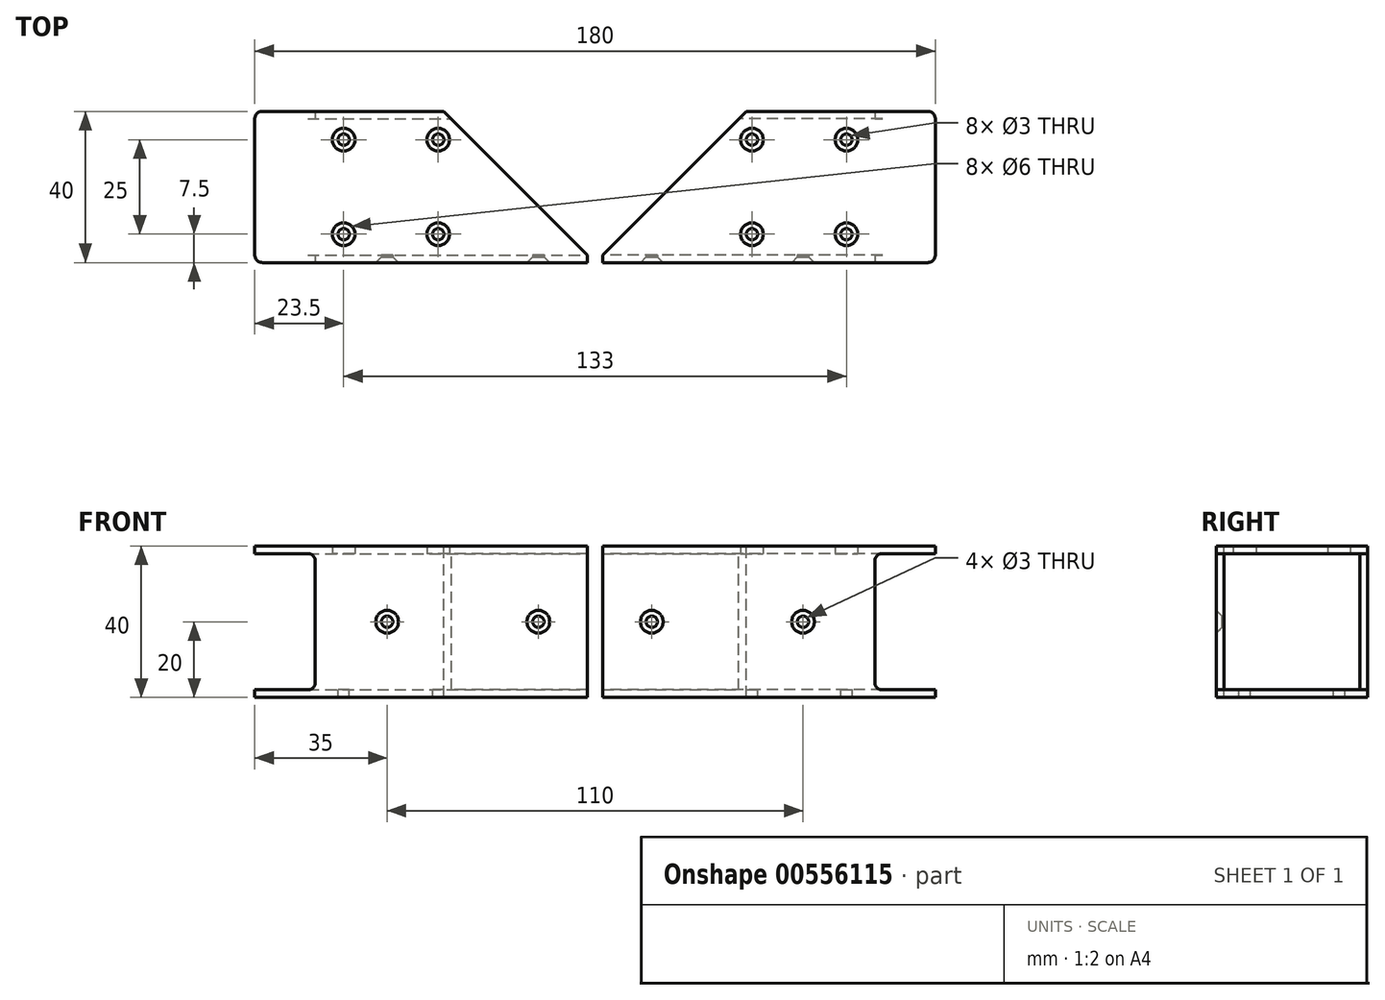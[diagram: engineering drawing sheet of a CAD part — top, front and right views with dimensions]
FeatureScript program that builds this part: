
annotation { "Feature Type Name" : "Feature", "Feature Type Description" : "" }
export const myFeature = defineFeature(function(context is Context, id is Id, definition is map)
    precondition{}
    {
        {
            var Q0;
            Q0=qCreatedBy(makeId("Right.planeOp"),FACE);
            var sketch = newSketch(context, id + "F0", { "sketchPlane" : qUnion([Q0])});
            skLineSegment(sketch, "E0.bottom", {"start": v(20, 20) * mm, "end": v(-20, 20) * mm});
            skLineSegment(sketch, "E0.top", {"start": v(20, -20) * mm, "end": v(-20, -20) * mm});
            skLineSegment(sketch, "E0.left", {"start": v(20, 20) * mm, "end": v(20, -20) * mm});
            skLineSegment(sketch, "E0.right", {"start": v(-20, 20) * mm, "end": v(-20, -20) * mm});
            skPoint(sketch, "E0.middle", {"position": v(0, 0) * mm});
            skSolve(sketch);
        }
        {
            var Q0;
            Q0=qSketchRegion(id+"F0",true);
            extrude(context, id + "F1", {"entities" : qUnion([Q0]), "oppositeDirection" : true, "depth" : 90 * mm, "offsetDistance" : 25 * mm});
        }
        {
            var Q0;
            Q0=makeQuery(id+"F1.opExtrude","CAP_FACE",FACE,{"disambiguationData":[OSD([sQuery(id+"F0.wireOp",EDGE,"E0.bottom"),sQuery(id+"F0.wireOp",EDGE,"E0.top"),sQuery(id+"F0.wireOp",EDGE,"E0.left"),sQuery(id+"F0.wireOp",EDGE,"E0.right")])],"isStart":false});
            var Q1;
            Q1=makeQuery(id+"F1.opExtrude","CAP_FACE",FACE,{"disambiguationData":[OSD([sQuery(id+"F0.wireOp",EDGE,"E0.bottom"),sQuery(id+"F0.wireOp",EDGE,"E0.top"),sQuery(id+"F0.wireOp",EDGE,"E0.left"),sQuery(id+"F0.wireOp",EDGE,"E0.right")])],"isStart":true});
            shell(context, id + "F2", {"entities" : qUnion([Q0, Q1]), "thickness" : 2 * mm});
        }
        {
            var Q0;
            Q0=makeQuery(id+"F2.opShell","OFFSET_FACE",FACE,{"disambiguationData":[OSD([sQuery(id+"F0.wireOp",EDGE,"E0.top")])]});
            var sketch = newSketch(context, id + "F3", { "sketchPlane" : qUnion([Q0])});
            skLineSegment(sketch, "E1", {"start": v(-90, 0) * mm, "end": v(0, 0) * mm, "construction": true});
            skLineSegment(sketch, "E2.bottom", {"start": v(-41.5, 12.5) * mm, "end": v(-66.5, 12.5) * mm, "construction": true});
            skLineSegment(sketch, "E2.top", {"start": v(-41.5, -12.5) * mm, "end": v(-66.5, -12.5) * mm, "construction": true});
            skLineSegment(sketch, "E2.left", {"start": v(-41.5, 12.5) * mm, "end": v(-41.5, -12.5) * mm, "construction": true});
            skLineSegment(sketch, "E2.right", {"start": v(-66.5, 12.5) * mm, "end": v(-66.5, -12.5) * mm, "construction": true});
            skPoint(sketch, "E2.middle", {"position": v(-54, 0) * mm});
            skLineSegment(sketch, "E3", {"start": v(-70, 18) * mm, "end": v(-70, -18) * mm, "construction": true});
            skSolve(sketch);
        }
        {
            var Q0;
            Q0=sQuery(id+"F3.wireOp",VERTEX,"E2.right.start");
            var Q1;
            Q1=sQuery(id+"F3.wireOp",VERTEX,"E2.top.end");
            var Q2;
            Q2=sQuery(id+"F3.wireOp",VERTEX,"E2.left.end");
            var Q3;
            Q3=sQuery(id+"F3.wireOp",VERTEX,"E2.left.start");
            var Q4;
            Q4=makeQuery(id+"F1.opExtrude","SWEPT_BODY",BODY,{"disambiguationData":[OSD([sQuery(id+"F0.wireOp",EDGE,"E0.bottom"),sQuery(id+"F0.wireOp",EDGE,"E0.top"),sQuery(id+"F0.wireOp",EDGE,"E0.left"),sQuery(id+"F0.wireOp",EDGE,"E0.right")])]});
            hole(context, id + "F4", {"style" : HoleStyle.SIMPLE, "endStyle" : HoleEndStyle.BLIND, "holeDiameter" : 3 * mm, "majorDiameter" : 5 * mm, "holeDepth" : 3 * mm, "isTappedThrough" : true, "tappedDepth" : 12 * mm, "tapClearance" : 3, "startFromSketch" : true, "locations" : qUnion([Q0, Q1, Q2, Q3]), "scope" : qUnion([Q4])});
        }
        {
            var Q0;
            Q0=sQuery(id+"F3.wireOp",VERTEX,"E2.right.start");
            var Q1;
            Q1=sQuery(id+"F3.wireOp",VERTEX,"E2.bottom.start");
            var Q2;
            Q2=sQuery(id+"F3.wireOp",VERTEX,"E2.top.end");
            var Q3;
            Q3=sQuery(id+"F3.wireOp",VERTEX,"E2.left.end");
            var Q4;
            Q4=makeQuery(id+"F1.opExtrude","SWEPT_BODY",BODY,{"disambiguationData":[OSD([sQuery(id+"F0.wireOp",EDGE,"E0.bottom"),sQuery(id+"F0.wireOp",EDGE,"E0.top"),sQuery(id+"F0.wireOp",EDGE,"E0.left"),sQuery(id+"F0.wireOp",EDGE,"E0.right")])]});
            hole(context, id + "F5", {"style" : HoleStyle.SIMPLE, "endStyle" : HoleEndStyle.BLIND, "oppositeDirection" : true, "holeDiameter" : 6 * mm, "majorDiameter" : 5 * mm, "holeDepth" : 40 * mm, "isTappedThrough" : true, "tappedDepth" : 12 * mm, "tapClearance" : 3, "locations" : qUnion([Q0, Q1, Q2, Q3]), "scope" : qUnion([Q4])});
        }
        {
            var Q0;
            Q0=makeQuery(id+"F1.opExtrude","SWEPT_FACE",FACE,{"disambiguationData":[OSD([sQuery(id+"F0.wireOp",EDGE,"E0.bottom")])]});
            var sketch = newSketch(context, id + "F6", { "sketchPlane" : qUnion([Q0])});
            skLineSegment(sketch, "E4", {"start": v(0, -20) * mm, "end": v(-40, 20) * mm});
            skLineSegment(sketch, "E5", {"start": v(-2, -20) * mm, "end": v(-2, -18) * mm});
            skSolve(sketch);
        }
        {
            var Q0;
            {var subQ1=sQuery(id+"F0.wireOp",EDGE,"E0.bottom");var subQ2=makeQuery(id+"F1.opExtrude","CAP_EDGE",EDGE,{"disambiguationData":[OSD([subQ1])],"isStart":true});Q0=makeQuery(id+"F6.imprint","IMPRINT",FACE,{"disambiguationData":[TD([[makeQuery(id+"F6.imprint","IMPRINT",EDGE,{"derivedFrom":subQ2}),-1.0]])]});}
            var Q1;
            {var subQ4=sQuery(id+"F6.wireOp",EDGE,"E5");Q1=makeQuery(id+"F6.imprint","IMPRINT",FACE,{"disambiguationData":[TD([[makeQuery(id+"F6.imprint","IMPRINT",EDGE,{"derivedFrom":subQ4}),-1.0]])]});}
            extrude(context, id + "F7", {"entities" : qUnion([Q0, Q1]), "operationType" : NewBodyOperationType.REMOVE, "endBound" : BoundingType.THROUGH_ALL, "oppositeDirection" : true, "depth" : 25 * mm, "offsetDistance" : 25 * mm});
        }
        {
            var Q0;
            Q0=makeQuery(id+"F1.opExtrude","SWEPT_FACE",FACE,{"disambiguationData":[OSD([sQuery(id+"F0.wireOp",EDGE,"E0.right")])]});
            var sketch = newSketch(context, id + "F8", { "sketchPlane" : qUnion([Q0])});
            skLineSegment(sketch, "E6", {"start": v(-70, -20) * mm, "end": v(-70, 20) * mm, "construction": true});
            skLineSegment(sketch, "E7", {"start": v(-70, 0) * mm, "end": v(-2, 0) * mm, "construction": true});
            skPoint(sketch, "E8", {"position": v(-55, 0) * mm});
            skPoint(sketch, "E9", {"position": v(-15, 0) * mm});
            skLineSegment(sketch, "E10.bottom", {"start": v(-90, -18) * mm, "end": v(-74, -18) * mm});
            skLineSegment(sketch, "E10.top", {"start": v(-90, 18) * mm, "end": v(-74, 18) * mm});
            skLineSegment(sketch, "E10.left", {"start": v(-90, -18) * mm, "end": v(-90, 18) * mm});
            skLineSegment(sketch, "E10.right", {"start": v(-74, -18) * mm, "end": v(-74, 18) * mm});
            skSolve(sketch);
        }
        {
            var Q0;
            Q0=makeQuery(id+"F8.imprint","IMPRINT",FACE,{"disambiguationData":[TD([[makeQuery(id+"F8.imprint","IMPRINT",EDGE,{"derivedFrom":sQuery(id+"F8.wireOp",EDGE,"E10.bottom")}),1.0]])]});
            extrude(context, id + "F9", {"entities" : qUnion([Q0]), "operationType" : NewBodyOperationType.REMOVE, "endBound" : BoundingType.THROUGH_ALL, "oppositeDirection" : true, "depth" : 25 * mm, "offsetDistance" : 25 * mm});
        }
        {
            var Q0;
            {var subQ0=sQuery(id+"F8.wireOp",EDGE,"E10.top");var subQ1=sQuery(id+"F0.wireOp",EDGE,"E0.right");var subQ2=sQuery(id+"F8.wireOp",EDGE,"E10.right");Q0=makeQuery(id+"F9.boolean.opBoolean","COPY",EDGE,{"disambiguationData":[TD([makeQuery(id+"F1.opExtrude","SWEPT_FACE",FACE,{"disambiguationData":[OSD([subQ1])]})])],"derivedFrom":makeQuery(id+"F9.opExtrude","SWEPT_EDGE",EDGE,{"disambiguationData":[OSD([subQ0,subQ2])]})});}
            var Q1;
            {var subQ0=sQuery(id+"F0.wireOp",EDGE,"E0.left");var subQ1=sQuery(id+"F8.wireOp",EDGE,"E10.top");var subQ2=sQuery(id+"F8.wireOp",EDGE,"E10.right");Q1=makeQuery(id+"F9.boolean.opBoolean","COPY",EDGE,{"disambiguationData":[TD([makeQuery(id+"F1.opExtrude","SWEPT_FACE",FACE,{"disambiguationData":[OSD([subQ0])]})])],"derivedFrom":makeQuery(id+"F9.opExtrude","SWEPT_EDGE",EDGE,{"disambiguationData":[OSD([subQ1,subQ2])]})});}
            var Q2;
            {var subQ0=sQuery(id+"F8.wireOp",EDGE,"E10.bottom");var subQ1=sQuery(id+"F0.wireOp",EDGE,"E0.left");var subQ2=sQuery(id+"F8.wireOp",EDGE,"E10.right");Q2=makeQuery(id+"F9.boolean.opBoolean","COPY",EDGE,{"disambiguationData":[TD([makeQuery(id+"F1.opExtrude","SWEPT_FACE",FACE,{"disambiguationData":[OSD([subQ1])]})])],"derivedFrom":makeQuery(id+"F9.opExtrude","SWEPT_EDGE",EDGE,{"disambiguationData":[OSD([subQ0,subQ2])]})});}
            var Q3;
            {var subQ0=sQuery(id+"F8.wireOp",EDGE,"E10.bottom");var subQ1=sQuery(id+"F0.wireOp",EDGE,"E0.right");var subQ2=sQuery(id+"F8.wireOp",EDGE,"E10.right");Q3=makeQuery(id+"F9.boolean.opBoolean","COPY",EDGE,{"disambiguationData":[TD([makeQuery(id+"F1.opExtrude","SWEPT_FACE",FACE,{"disambiguationData":[OSD([subQ1])]})])],"derivedFrom":makeQuery(id+"F9.opExtrude","SWEPT_EDGE",EDGE,{"disambiguationData":[OSD([subQ0,subQ2])]})});}
            var Q4;
            {var subQ0=sQuery(id+"F0.wireOp",EDGE,"E0.bottom");var subQ1=sQuery(id+"F0.wireOp",EDGE,"E0.left");Q4=makeQuery(id+"F9.boolean.opBoolean","SPLIT",EDGE,{"disambiguationData":[TD([makeQuery(id+"F1.opExtrude","SWEPT_FACE",FACE,{"disambiguationData":[OSD([subQ0])]})])],"derivedFrom":makeQuery(id+"F1.opExtrude","CAP_EDGE",EDGE,{"disambiguationData":[OSD([subQ1])],"isStart":false})});}
            var Q5;
            {var subQ0=sQuery(id+"F0.wireOp",EDGE,"E0.bottom");var subQ1=sQuery(id+"F0.wireOp",EDGE,"E0.right");Q5=makeQuery(id+"F9.boolean.opBoolean","SPLIT",EDGE,{"disambiguationData":[TD([makeQuery(id+"F1.opExtrude","SWEPT_FACE",FACE,{"disambiguationData":[OSD([subQ0])]})])],"derivedFrom":makeQuery(id+"F1.opExtrude","CAP_EDGE",EDGE,{"disambiguationData":[OSD([subQ1])],"isStart":false})});}
            var Q6;
            {var subQ0=sQuery(id+"F0.wireOp",EDGE,"E0.right");var subQ1=sQuery(id+"F0.wireOp",EDGE,"E0.top");Q6=makeQuery(id+"F9.boolean.opBoolean","SPLIT",EDGE,{"disambiguationData":[TD([makeQuery(id+"F1.opExtrude","SWEPT_FACE",FACE,{"disambiguationData":[OSD([subQ1])]})])],"derivedFrom":makeQuery(id+"F1.opExtrude","CAP_EDGE",EDGE,{"disambiguationData":[OSD([subQ0])],"isStart":false})});}
            var Q7;
            {var subQ0=sQuery(id+"F0.wireOp",EDGE,"E0.left");var subQ1=sQuery(id+"F0.wireOp",EDGE,"E0.top");Q7=makeQuery(id+"F9.boolean.opBoolean","SPLIT",EDGE,{"disambiguationData":[TD([makeQuery(id+"F1.opExtrude","SWEPT_FACE",FACE,{"disambiguationData":[OSD([subQ1])]})])],"derivedFrom":makeQuery(id+"F1.opExtrude","CAP_EDGE",EDGE,{"disambiguationData":[OSD([subQ0])],"isStart":false})});}
            fillet(context, id + "F10", {"entities" : qUnion([Q0, Q1, Q2, Q3, Q4, Q5, Q6, Q7]), "radius" : 2 * mm, "tangentPropagation" : true, "allowEdgeOverflow" : false});
        }
        {
            var Q0;
            Q0=sQuery(id+"F8.wireOp",VERTEX,"E8");
            var Q1;
            Q1=sQuery(id+"F8.wireOp",VERTEX,"E9");
            var Q2;
            Q2=makeQuery(id+"F1.opExtrude","SWEPT_BODY",BODY,{"disambiguationData":[OSD([sQuery(id+"F0.wireOp",EDGE,"E0.bottom"),sQuery(id+"F0.wireOp",EDGE,"E0.top"),sQuery(id+"F0.wireOp",EDGE,"E0.left"),sQuery(id+"F0.wireOp",EDGE,"E0.right")])]});
            hole(context, id + "F11", {"style" : HoleStyle.C_SINK, "endStyle" : HoleEndStyle.BLIND, "holeDiameter" : 3 * mm, "cSinkDiameter" : 6 * mm, "cSinkAngle" : 90 * degree, "majorDiameter" : 5 * mm, "holeDepth" : 3 * mm, "isTappedThrough" : true, "tappedDepth" : 12 * mm, "tapClearance" : 3, "startFromSketch" : true, "locations" : qUnion([Q0, Q1]), "scope" : qUnion([Q2])});
        }
        {
            var Q0;
            Q0=makeQuery(id+"F1.opExtrude","SWEPT_BODY",BODY,{"disambiguationData":[OSD([sQuery(id+"F0.wireOp",EDGE,"E0.bottom"),sQuery(id+"F0.wireOp",EDGE,"E0.top"),sQuery(id+"F0.wireOp",EDGE,"E0.left"),sQuery(id+"F0.wireOp",EDGE,"E0.right")])]});
            var Q1;
            Q1=qCreatedBy(makeId("Right.planeOp"),FACE);
            mirror(context, id + "F12", {"entities" : qUnion([Q0]), "mirrorPlane" : qUnion([Q1])});
        }
    });
